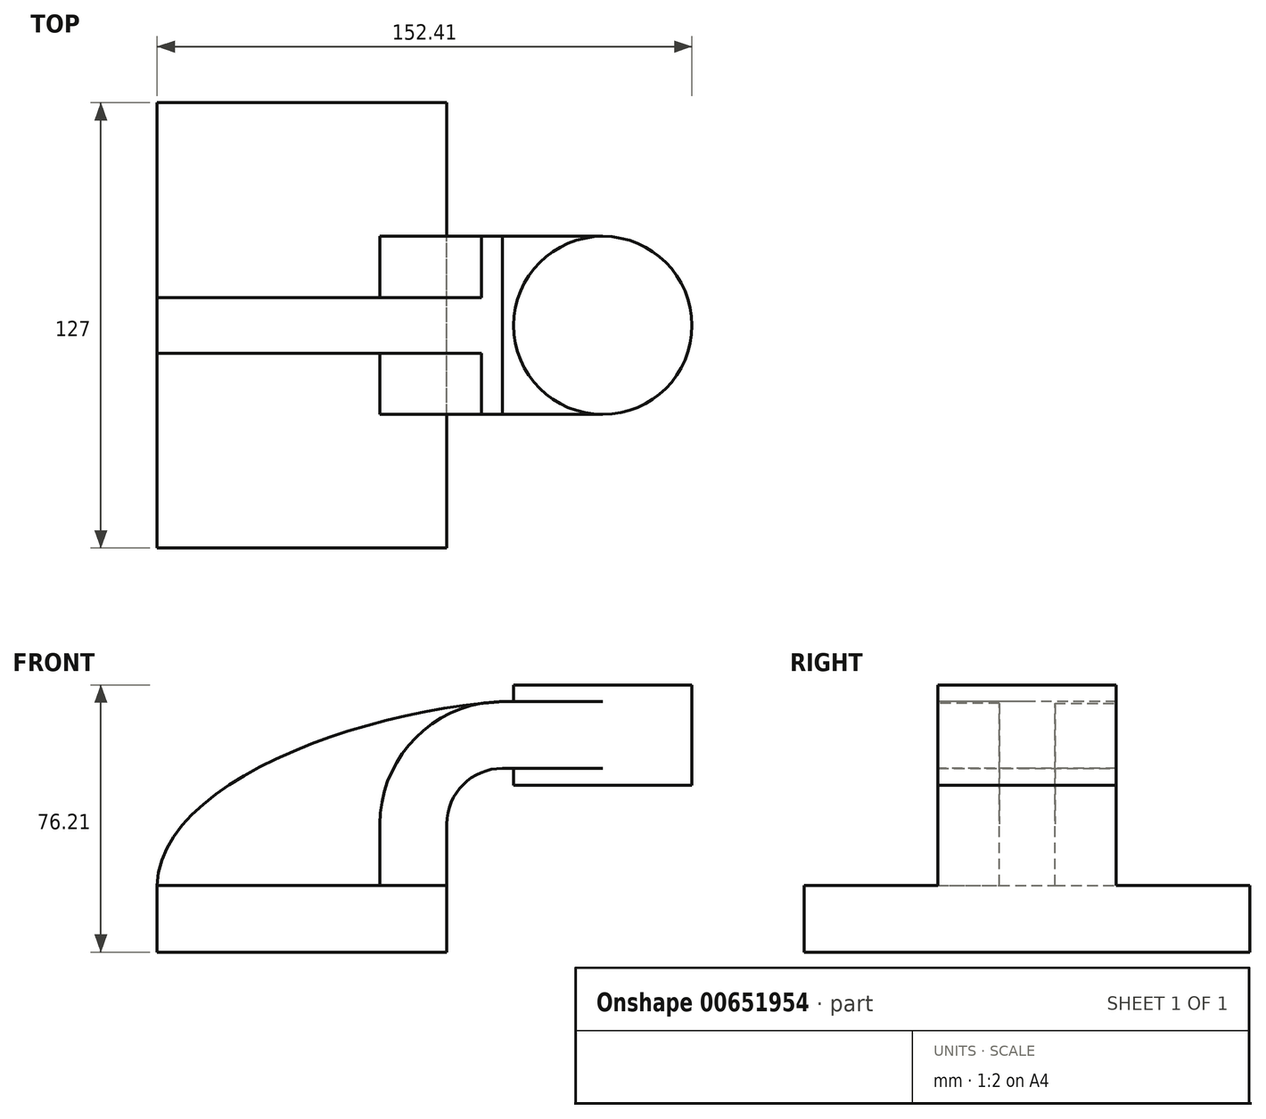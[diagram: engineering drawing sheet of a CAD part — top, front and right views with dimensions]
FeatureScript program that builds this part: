
annotation { "Feature Type Name" : "Feature", "Feature Type Description" : "" }
export const myFeature = defineFeature(function(context is Context, id is Id, definition is map)
    precondition{}
    {
        {
            var Q0;
            Q0=qCreatedBy(makeId("Front.planeOp"),FACE);
            var sketch = newSketch(context, id + "F0", { "sketchPlane" : qUnion([Q0])});
            skLineSegment(sketch, "E0.bottom", {"start": v(-41.28, 9.52) * mm, "end": v(41.28, 9.53) * mm});
            skLineSegment(sketch, "E0.top", {"start": v(-41.28, -9.53) * mm, "end": v(41.28, -9.53) * mm});
            skLineSegment(sketch, "E0.left", {"start": v(-41.28, 9.52) * mm, "end": v(-41.27, -9.53) * mm});
            skLineSegment(sketch, "E0.right", {"start": v(41.28, 9.53) * mm, "end": v(41.28, -9.52) * mm});
            skPoint(sketch, "E0.middle", {"position": v(0, 0) * mm});
            skLineSegment(sketch, "E1", {"start": v(41.27, 9.53) * mm, "end": v(41.27, 27) * mm});
            skLineSegment(sketch, "E2.bottom", {"start": v(60.32, 38.1) * mm, "end": v(111.12, 38.1) * mm});
            skLineSegment(sketch, "E2.top", {"start": v(60.32, 66.68) * mm, "end": v(111.12, 66.68) * mm});
            skLineSegment(sketch, "E2.left", {"start": v(60.32, 38.1) * mm, "end": v(60.32, 66.67) * mm});
            skLineSegment(sketch, "E2.right", {"start": v(111.13, 38.1) * mm, "end": v(111.13, 66.67) * mm});
            skPoint(sketch, "E2.middle", {"position": v(85.72, 52.39) * mm});
            skArc(sketch, "E3", {"start": v(41.27, 27) * mm, "mid": v(45.92, 38.23) * mm, "end": v(57.15, 42.88) * mm});
            skLineSegment(sketch, "E4", {"start": v(57.15, 42.88) * mm, "end": v(85.72, 42.88) * mm});
            skPoint(sketch, "E4.endSnap0", {"position": v(85.72, 38.1) * mm});
            skLineSegment(sketch, "E5.0", {"start": v(57.15, 61.93) * mm, "end": v(85.72, 61.93) * mm});
            skArc(sketch, "E5.1", {"start": v(22.22, 27) * mm, "mid": v(32.45, 51.7) * mm, "end": v(57.15, 61.93) * mm});
            skLineSegment(sketch, "E5.2", {"start": v(22.22, 9.53) * mm, "end": v(22.22, 27) * mm});
            skLineSegment(sketch, "E6", {"start": v(85.72, 42.88) * mm, "end": v(85.72, 66.68) * mm});
            skFitSpline(sketch, "E7", {"points": [v(-41.28, 9.53) * mm, v(57.15, 61.93) * mm], "startDerivative": vector(2.66, 88.45) * mm, "endDerivative": vector(121.8, 8.24) * mm});
            skLineSegment(sketch, "E8", {"start": v(85.72, 38.1) * mm, "end": v(85.72, 42.88) * mm});
            skSolve(sketch);
        }
        {
            var Q0;
            Q0=makeQuery(id+"F0.imprint","IMPRINT",FACE,{"disambiguationData":[TD([[makeQuery(id+"F0.imprint","IMPRINT",EDGE,{"derivedFrom":sQuery(id+"F0.wireOp",EDGE,"E0.top")}),1.0]])]});
            extrude(context, id + "F1", {"entities" : qUnion([Q0]), "endBound" : BoundingType.SYMMETRIC, "depth" : 127 * mm, "offsetDistance" : 25.4 * mm});
        }
        {
            var Q0;
            {var subQ10=sQuery(id+"F0.wireOp",EDGE,"E1");Q0=makeQuery(id+"F0.imprint","IMPRINT",FACE,{"disambiguationData":[TD([[makeQuery(id+"F0.imprint","IMPRINT",EDGE,{"derivedFrom":subQ10}),1.0]])]});}
            var Q1;
            {var subQ0=sQuery(id+"F0.wireOp",EDGE,"E4");var subQ1=sQuery(id+"F0.wireOp",EDGE,"E2.left");var subQ2=makeQuery(id+"F0.imprint","INTERSECT",VERTEX,{"derivedFrom":[subQ1,subQ0]});Q1=makeQuery(id+"F0.imprint","IMPRINT",FACE,{"disambiguationData":[TD([[makeQuery(id+"F0.imprint","IMPRINT",EDGE,{"disambiguationData":[TD([[subQ2,-1.0]])],"derivedFrom":subQ1}),-1.0]])]});}
            extrude(context, id + "F2", {"entities" : qUnion([Q0, Q1]), "operationType" : NewBodyOperationType.ADD, "endBound" : BoundingType.SYMMETRIC, "depth" : 50.8 * mm, "offsetDistance" : 25.4 * mm});
        }
        {
            var Q0;
            {var subQ3=sQuery(id+"F0.wireOp",EDGE,"E5.2");Q0=makeQuery(id+"F0.imprint","IMPRINT",FACE,{"disambiguationData":[TD([[makeQuery(id+"F0.imprint","IMPRINT",EDGE,{"derivedFrom":subQ3}),1.0]])]});}
            extrude(context, id + "F3", {"entities" : qUnion([Q0]), "operationType" : NewBodyOperationType.ADD, "endBound" : BoundingType.SYMMETRIC, "depth" : 15.88 * mm, "offsetDistance" : 25.4 * mm});
        }
        {
            var Q0;
            {var subQ0=sQuery(id+"F0.wireOp",EDGE,"E2.right");Q0=makeQuery(id+"F0.imprint","IMPRINT",FACE,{"disambiguationData":[TD([[makeQuery(id+"F0.imprint","IMPRINT",EDGE,{"derivedFrom":subQ0}),1.0]])]});}
            var Q1;
            Q1=sQuery(id+"F0.wireOp",EDGE,"E6");
            revolve(context, id + "F4", {"operationType" : NewBodyOperationType.ADD, "entities" : qUnion([Q0]), "axis" : qUnion([Q1]), "revolveType" : RevolveType.FULL});
        }
    });
